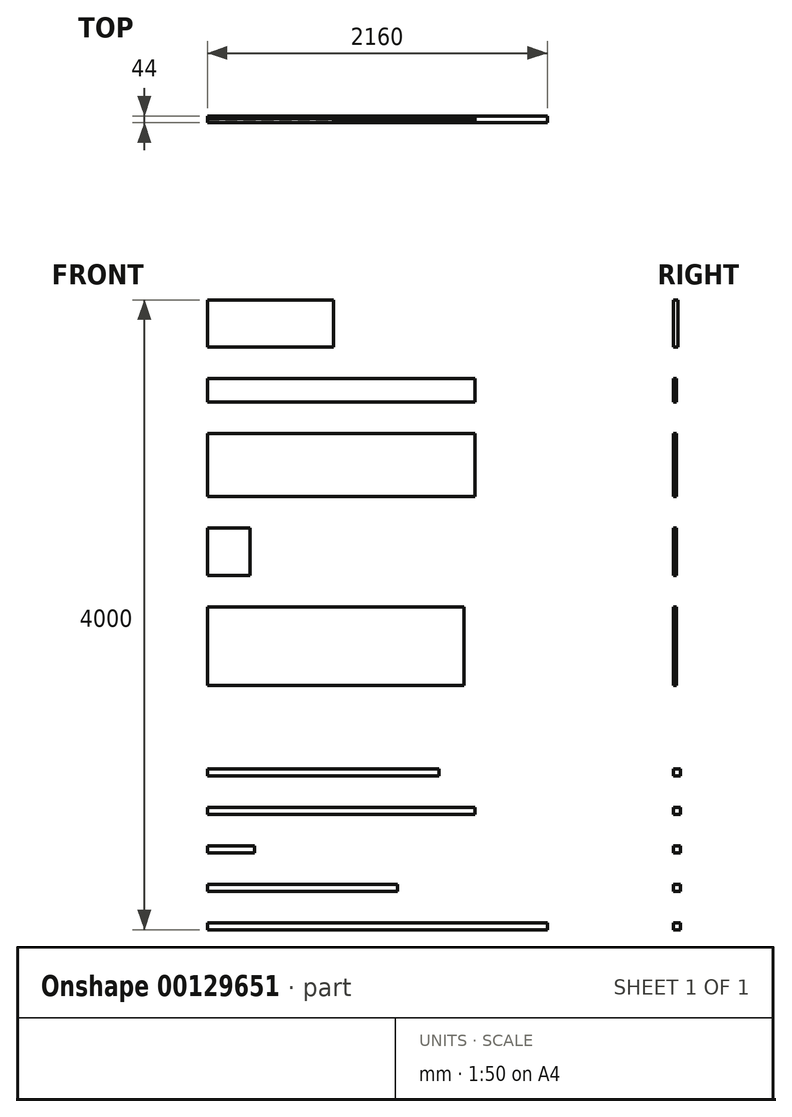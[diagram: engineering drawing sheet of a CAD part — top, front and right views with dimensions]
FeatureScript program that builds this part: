
annotation { "Feature Type Name" : "Feature", "Feature Type Description" : "" }
export const myFeature = defineFeature(function(context is Context, id is Id, definition is map)
    precondition{}
    {
        {
            assignVariable(context, id + "F0", {"name" : "Dicke", "anyValue" : 44});
        }
        {
            var Q0;
            Q0=qCreatedBy(makeId("Front.planeOp"),FACE);
            var sketch = newSketch(context, id + "F1", { "sketchPlane" : qUnion([Q0])});
            skLineSegment(sketch, "E0.bottom", {"start": v(0, 0) * mm, "end": v(2160, 0) * mm});
            skLineSegment(sketch, "E0.top", {"start": v(0, 44) * mm, "end": v(2160, 44) * mm});
            skLineSegment(sketch, "E0.left", {"start": v(0, 0) * mm, "end": v(0, 44) * mm});
            skLineSegment(sketch, "E0.right", {"start": v(2160, 0) * mm, "end": v(2160, 44) * mm});
            skLineSegment(sketch, "E1", {"start": v(0, 0) * mm, "end": v(0, 4000) * mm, "construction": true});
            skLineSegment(sketch, "E2.bottom", {"start": v(0, 4000) * mm, "end": v(800, 4000) * mm});
            skLineSegment(sketch, "E2.top", {"start": v(0, 3700) * mm, "end": v(800, 3700) * mm});
            skLineSegment(sketch, "E2.left", {"start": v(0, 4000) * mm, "end": v(0, 3700) * mm});
            skLineSegment(sketch, "E2.right", {"start": v(800, 4000) * mm, "end": v(800, 3700) * mm});
            skLineSegment(sketch, "E3.bottom", {"start": v(0, 3500) * mm, "end": v(1700, 3500) * mm});
            skLineSegment(sketch, "E3.top", {"start": v(0, 3350) * mm, "end": v(1700, 3350) * mm});
            skLineSegment(sketch, "E3.left", {"start": v(0, 3500) * mm, "end": v(0, 3350) * mm});
            skLineSegment(sketch, "E3.right", {"start": v(1700, 3500) * mm, "end": v(1700, 3350) * mm});
            skLineSegment(sketch, "E4.bottom", {"start": v(0, 3150) * mm, "end": v(1700, 3150) * mm});
            skLineSegment(sketch, "E4.top", {"start": v(0, 2750) * mm, "end": v(1700, 2750) * mm});
            skLineSegment(sketch, "E4.left", {"start": v(0, 3150) * mm, "end": v(0, 2750) * mm});
            skLineSegment(sketch, "E4.right", {"start": v(1700, 3150) * mm, "end": v(1700, 2750) * mm});
            skLineSegment(sketch, "E5.bottom", {"start": v(0, 244) * mm, "end": v(1208, 244) * mm});
            skLineSegment(sketch, "E5.top", {"start": v(0, 288) * mm, "end": v(1208, 288) * mm});
            skLineSegment(sketch, "E5.left", {"start": v(0, 244) * mm, "end": v(0, 288) * mm});
            skLineSegment(sketch, "E5.right", {"start": v(1208, 244) * mm, "end": v(1208, 288) * mm});
            skLineSegment(sketch, "E6.bottom", {"start": v(0, 2550) * mm, "end": v(270, 2550) * mm});
            skLineSegment(sketch, "E6.top", {"start": v(0, 2250) * mm, "end": v(270, 2250) * mm});
            skLineSegment(sketch, "E6.left", {"start": v(0, 2550) * mm, "end": v(0, 2250) * mm});
            skLineSegment(sketch, "E6.right", {"start": v(270, 2550) * mm, "end": v(270, 2250) * mm});
            skLineSegment(sketch, "E7.bottom", {"start": v(0, 488) * mm, "end": v(300, 488) * mm});
            skLineSegment(sketch, "E7.top", {"start": v(0, 532) * mm, "end": v(300, 532) * mm});
            skLineSegment(sketch, "E7.left", {"start": v(0, 488) * mm, "end": v(0, 532) * mm});
            skLineSegment(sketch, "E7.right", {"start": v(300, 488) * mm, "end": v(300, 532) * mm});
            skLineSegment(sketch, "E8.bottom", {"start": v(0, 2050) * mm, "end": v(1630, 2050) * mm});
            skLineSegment(sketch, "E8.top", {"start": v(0, 1550) * mm, "end": v(1630, 1550) * mm});
            skLineSegment(sketch, "E8.left", {"start": v(0, 2050) * mm, "end": v(0, 1550) * mm});
            skLineSegment(sketch, "E8.right", {"start": v(1630, 2050) * mm, "end": v(1630, 1550) * mm});
            skLineSegment(sketch, "E9.bottom", {"start": v(0, 776) * mm, "end": v(1700, 776) * mm});
            skLineSegment(sketch, "E9.top", {"start": v(0, 732) * mm, "end": v(1700, 732) * mm});
            skLineSegment(sketch, "E9.left", {"start": v(0, 776) * mm, "end": v(0, 732) * mm});
            skLineSegment(sketch, "E9.right", {"start": v(1700, 776) * mm, "end": v(1700, 732) * mm});
            skLineSegment(sketch, "E10.bottom", {"start": v(0, 1020) * mm, "end": v(1472, 1020) * mm});
            skLineSegment(sketch, "E10.top", {"start": v(0, 976) * mm, "end": v(1472, 976) * mm});
            skLineSegment(sketch, "E10.left", {"start": v(0, 1020) * mm, "end": v(0, 976) * mm});
            skLineSegment(sketch, "E10.right", {"start": v(1472, 1020) * mm, "end": v(1472, 976) * mm});
            skSolve(sketch);
        }
        {
            var Q0;
            Q0=makeQuery(id+"F1.imprint","IMPRINT",FACE,{"disambiguationData":[TD([[makeQuery(id+"F1.imprint","IMPRINT",EDGE,{"derivedFrom":sQuery(id+"F1.wireOp",EDGE,"E0.bottom")}),1.0]])]});
            extrude(context, id + "F2", {"entities" : qUnion([Q0]), "oppositeDirection" : true, "depth" : (getVariable(context, 'Dicke')) * mm});
        }
        {
            var Q0;
            Q0=makeQuery(id+"F1.imprint","IMPRINT",FACE,{"disambiguationData":[TD([[makeQuery(id+"F1.imprint","IMPRINT",EDGE,{"derivedFrom":sQuery(id+"F1.wireOp",EDGE,"E2.bottom")}),-1.0]])]});
            extrude(context, id + "F3", {"entities" : qUnion([Q0]), "oppositeDirection" : true, "depth" : 28 * mm, "offsetDistance" : 25 * mm});
        }
        {
            var Q0;
            Q0=makeQuery(id+"F1.imprint","IMPRINT",FACE,{"disambiguationData":[TD([[makeQuery(id+"F1.imprint","IMPRINT",EDGE,{"derivedFrom":sQuery(id+"F1.wireOp",EDGE,"E3.bottom")}),-1.0]])]});
            extrude(context, id + "F4", {"entities" : qUnion([Q0]), "oppositeDirection" : true, "depth" : 20 * mm});
        }
        {
            var Q0;
            Q0=makeQuery(id+"F1.imprint","IMPRINT",FACE,{"disambiguationData":[TD([[makeQuery(id+"F1.imprint","IMPRINT",EDGE,{"derivedFrom":sQuery(id+"F1.wireOp",EDGE,"E4.bottom")}),-1.0]])]});
            extrude(context, id + "F5", {"entities" : qUnion([Q0]), "oppositeDirection" : true, "depth" : 20 * mm});
        }
        {
            var Q0;
            Q0=makeQuery(id+"F1.imprint","IMPRINT",FACE,{"disambiguationData":[TD([[makeQuery(id+"F1.imprint","IMPRINT",EDGE,{"derivedFrom":sQuery(id+"F1.wireOp",EDGE,"E5.bottom")}),1.0]])]});
            extrude(context, id + "F6", {"entities" : qUnion([Q0]), "oppositeDirection" : true, "depth" : (getVariable(context, 'Dicke')) * mm, "offsetDistance" : 25 * mm});
        }
        {
            var Q0;
            Q0=makeQuery(id+"F1.imprint","IMPRINT",FACE,{"disambiguationData":[TD([[makeQuery(id+"F1.imprint","IMPRINT",EDGE,{"derivedFrom":sQuery(id+"F1.wireOp",EDGE,"E6.bottom")}),-1.0]])]});
            extrude(context, id + "F7", {"entities" : qUnion([Q0]), "oppositeDirection" : true, "depth" : 20 * mm});
        }
        {
            var Q0;
            Q0=makeQuery(id+"F1.imprint","IMPRINT",FACE,{"disambiguationData":[TD([[makeQuery(id+"F1.imprint","IMPRINT",EDGE,{"derivedFrom":sQuery(id+"F1.wireOp",EDGE,"E7.bottom")}),1.0]])]});
            extrude(context, id + "F8", {"entities" : qUnion([Q0]), "oppositeDirection" : true, "depth" : (getVariable(context, 'Dicke')) * mm, "offsetDistance" : 25 * mm});
        }
        {
            var Q0;
            Q0=makeQuery(id+"F1.imprint","IMPRINT",FACE,{"disambiguationData":[TD([[makeQuery(id+"F1.imprint","IMPRINT",EDGE,{"derivedFrom":sQuery(id+"F1.wireOp",EDGE,"E8.bottom")}),-1.0]])]});
            extrude(context, id + "F9", {"entities" : qUnion([Q0]), "oppositeDirection" : true, "depth" : 20 * mm});
        }
        {
            var Q0;
            Q0=makeQuery(id+"F1.imprint","IMPRINT",FACE,{"disambiguationData":[TD([[makeQuery(id+"F1.imprint","IMPRINT",EDGE,{"derivedFrom":sQuery(id+"F1.wireOp",EDGE,"E9.bottom")}),-1.0]])]});
            extrude(context, id + "F10", {"entities" : qUnion([Q0]), "oppositeDirection" : true, "depth" : (getVariable(context, 'Dicke')) * mm, "offsetDistance" : 25 * mm});
        }
        {
            var Q0;
            Q0=makeQuery(id+"F1.imprint","IMPRINT",FACE,{"disambiguationData":[TD([[makeQuery(id+"F1.imprint","IMPRINT",EDGE,{"derivedFrom":sQuery(id+"F1.wireOp",EDGE,"E10.bottom")}),-1.0]])]});
            extrude(context, id + "F11", {"entities" : qUnion([Q0]), "oppositeDirection" : true, "depth" : (getVariable(context, 'Dicke')) * mm, "offsetDistance" : 25 * mm});
        }
    });
